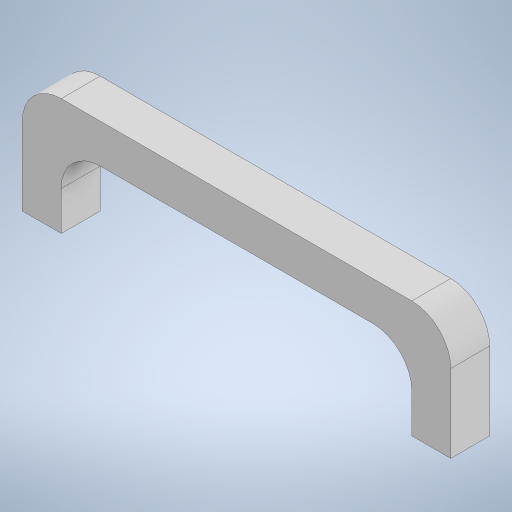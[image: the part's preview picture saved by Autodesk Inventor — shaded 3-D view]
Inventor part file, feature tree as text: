
AUTODESK INVENTOR PART (.ipt)
format: ipt  version: 2023 (Build 270158000, 158)  size: 252,928 bytes
history: native  units: in
note: dims shown in document units (in); Inventor stores cm internally (conversion verified against a paired STEP export)
features: extrude x2, sketch x2, fillet x1
ambient origin geometry x8: Origin, YZ Plane, XZ Plane, XY Plane, X Axis, Y Axis, Z Axis, Center Point
bodies: Solid1 (feature_tree)
feature tree (5):
  extrude  "Extrusion1"  Depth=1.1811in
  fillet  "Fillet1"  Radius=0.3937in
  extrude  "Extrusion2"  Depth=0.3937in
  sketch  "Sketch1"  dims[d0=4.3307in d1=1.1811in d2=0.3937in]
  sketch  "Sketch2"  dims[d3=0.3937in d4=0.3937in d5=0.3937in d6=0.0in d7=0.3937in d8=0.1969in d9=0.1969in d10=0.1654in d11=0.1969in d12=0.1969in d13=0.1654in d14=0.5906in d15=0.0in]
